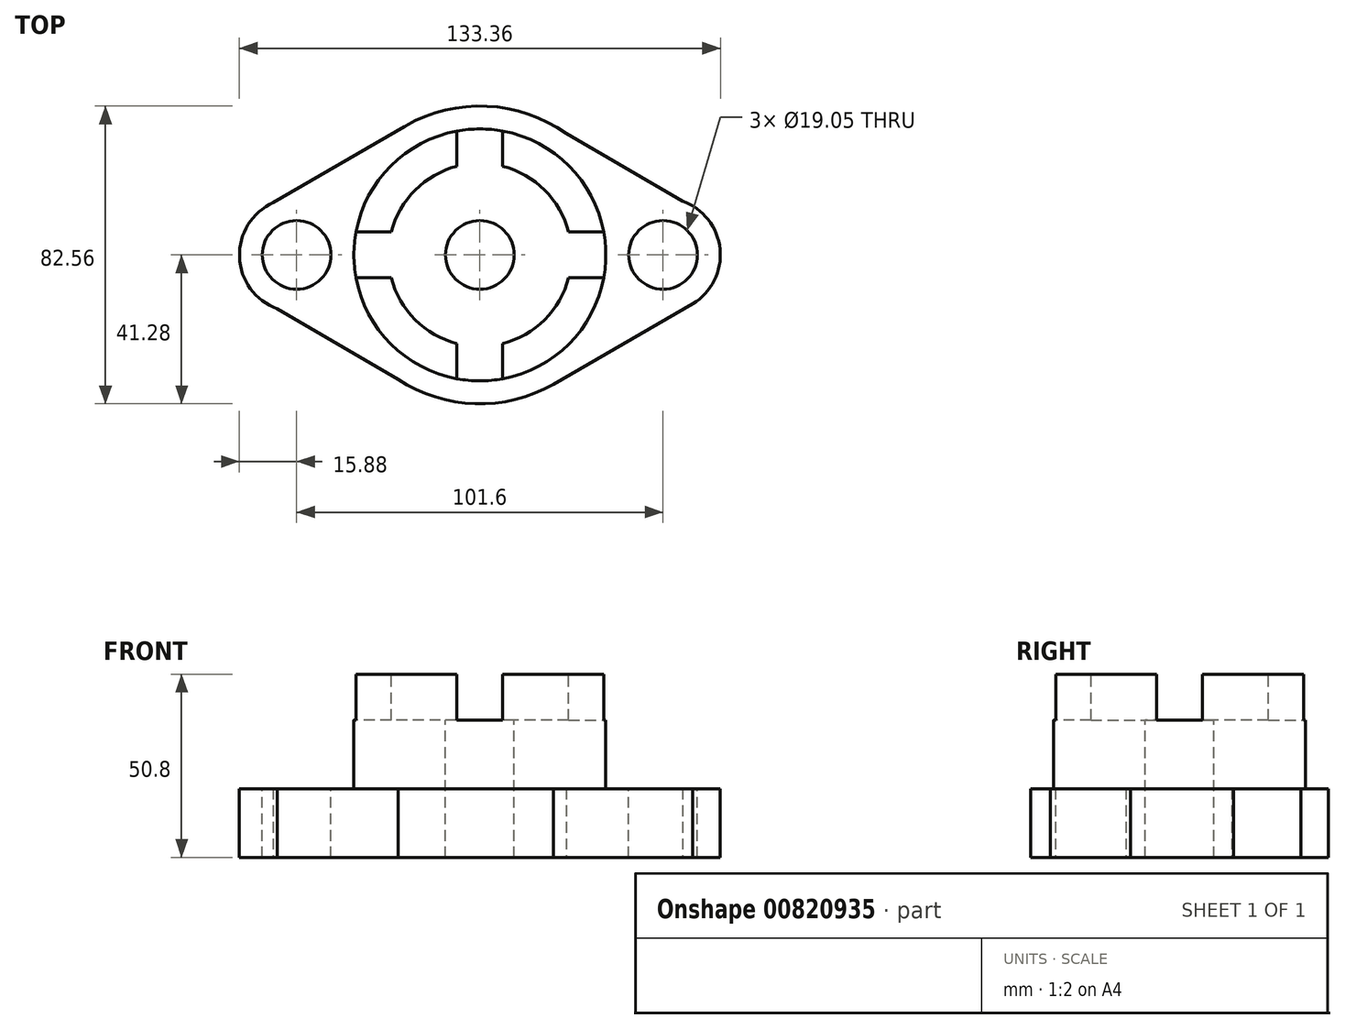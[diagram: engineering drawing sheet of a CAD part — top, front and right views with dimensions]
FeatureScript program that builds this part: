
annotation { "Feature Type Name" : "Feature", "Feature Type Description" : "" }
export const myFeature = defineFeature(function(context is Context, id is Id, definition is map)
    precondition{}
    {
        {
            var Q0;
            Q0=qCreatedBy(makeId("Top.planeOp"),FACE);
            var sketch = newSketch(context, id + "F0", { "sketchPlane" : qUnion([Q0])});
            skCircle(sketch, "E0", {"center": v(0, 0) * mm, "radius": 41.28 * mm});
            skSolve(sketch);
        }
        {
            var Q0;
            Q0=qCreatedBy(makeId("Top.planeOp"),FACE);
            var sketch = newSketch(context, id + "F1", { "sketchPlane" : qUnion([Q0])});
            skCircle(sketch, "E1", {"center": v(-50.8, 0) * mm, "radius": 15.88 * mm});
            skCircle(sketch, "E2", {"center": v(50.8, 0) * mm, "radius": 15.88 * mm});
            skSolve(sketch);
        }
        {
            var Q0;
            Q0=qCreatedBy(makeId("Top.planeOp"),FACE);
            var sketch = newSketch(context, id + "F2", { "sketchPlane" : qUnion([Q0])});
            skLineSegment(sketch, "E3", {"start": v(-60.13, 12.85) * mm, "end": v(-20.59, 35.77) * mm});
            skLineSegment(sketch, "E4", {"start": v(-20.59, 35.77) * mm, "end": v(-27.6, 7.86) * mm});
            skLineSegment(sketch, "E5", {"start": v(-27.6, 7.86) * mm, "end": v(-60.13, 12.85) * mm});
            skSolve(sketch);
        }
        {
            var Q0;
            Q0=qCreatedBy(makeId("Top.planeOp"),FACE);
            var sketch = newSketch(context, id + "F3", { "sketchPlane" : qUnion([Q0])});
            skLineSegment(sketch, "E6", {"start": v(-60.23, -12.58) * mm, "end": v(-21.62, -35.1) * mm});
            skLineSegment(sketch, "E7", {"start": v(-60.23, -12.58) * mm, "end": v(-30.25, -6.15) * mm});
            skLineSegment(sketch, "E8", {"start": v(-30.25, -6.15) * mm, "end": v(-21.62, -35.1) * mm});
            skSolve(sketch);
        }
        {
            var Q0;
            Q0=qCreatedBy(makeId("Top.planeOp"),FACE);
            var sketch = newSketch(context, id + "F4", { "sketchPlane" : qUnion([Q0])});
            skLineSegment(sketch, "E9", {"start": v(17.34, 37.46) * mm, "end": v(58.42, 13.63) * mm});
            skLineSegment(sketch, "E10", {"start": v(17.34, 37.46) * mm, "end": v(25.2, 3.74) * mm});
            skLineSegment(sketch, "E11", {"start": v(25.2, 3.74) * mm, "end": v(58.42, 13.63) * mm});
            skSolve(sketch);
        }
        {
            var Q0;
            Q0=qCreatedBy(makeId("Top.planeOp"),FACE);
            var sketch = newSketch(context, id + "F5", { "sketchPlane" : qUnion([Q0])});
            skLineSegment(sketch, "E12", {"start": v(16.99, -37.85) * mm, "end": v(60.11, -12.95) * mm});
            skLineSegment(sketch, "E13", {"start": v(20.37, -35.9) * mm, "end": v(28.45, -4.63) * mm});
            skLineSegment(sketch, "E14", {"start": v(28.45, -4.63) * mm, "end": v(59, -13.6) * mm});
            skSolve(sketch);
        }
        {
            var Q0;
            Q0=makeQuery(id+"F2.imprint","IMPRINT",FACE,{"disambiguationData":[TD([[makeQuery(id+"F2.imprint","IMPRINT",EDGE,{"derivedFrom":sQuery(id+"F2.wireOp",EDGE,"E3")}),-1.0]])]});
            var Q1;
            Q1=makeQuery(id+"F1.imprint","IMPRINT",FACE,{"disambiguationData":[TD([[makeQuery(id+"F1.imprint","IMPRINT",EDGE,{"derivedFrom":sQuery(id+"F1.wireOp",EDGE,"E1")}),1.0]])]});
            var Q2;
            Q2=makeQuery(id+"F0.imprint","IMPRINT",FACE,{"disambiguationData":[TD([[makeQuery(id+"F0.imprint","IMPRINT",EDGE,{"derivedFrom":sQuery(id+"F0.wireOp",EDGE,"E0")}),1.0]])]});
            var Q3;
            Q3=makeQuery(id+"F3.imprint","IMPRINT",FACE,{"disambiguationData":[TD([[makeQuery(id+"F3.imprint","IMPRINT",EDGE,{"derivedFrom":sQuery(id+"F3.wireOp",EDGE,"E6")}),1.0]])]});
            var Q4;
            Q4=makeQuery(id+"F4.imprint","IMPRINT",FACE,{"disambiguationData":[TD([[makeQuery(id+"F4.imprint","IMPRINT",EDGE,{"derivedFrom":sQuery(id+"F4.wireOp",EDGE,"E9")}),-1.0]])]});
            var Q5;
            Q5=makeQuery(id+"F1.imprint","IMPRINT",FACE,{"disambiguationData":[TD([[makeQuery(id+"F1.imprint","IMPRINT",EDGE,{"derivedFrom":sQuery(id+"F1.wireOp",EDGE,"E2")}),1.0]])]});
            var Q6;
            {var subQ0=sQuery(id+"F5.wireOp",EDGE,"E13");Q6=makeQuery(id+"F5.imprint","IMPRINT",FACE,{"disambiguationData":[TD([[makeQuery(id+"F5.imprint","IMPRINT",EDGE,{"derivedFrom":subQ0}),-1.0]])]});}
            extrude(context, id + "F6", {"entities" : qUnion([Q0, Q1, Q2, Q3, Q4, Q5, Q6]), "depth" : 19.05 * mm, "offsetDistance" : 25.4 * mm});
        }
        {
            var Q0;
            Q0=makeQuery(id+"F6.opExtrude","SWEPT_BODY",BODY,{"disambiguationData":[OSD([sQuery(id+"F2.wireOp",EDGE,"E3"),sQuery(id+"F2.wireOp",EDGE,"E4"),sQuery(id+"F2.wireOp",EDGE,"E5")])]});
            var Q1;
            Q1=makeQuery(id+"F6.opExtrude","SWEPT_BODY",BODY,{"disambiguationData":[OSD([sQuery(id+"F0.wireOp",EDGE,"E0")])]});
            var Q2;
            Q2=makeQuery(id+"F6.opExtrude","SWEPT_BODY",BODY,{"disambiguationData":[OSD([sQuery(id+"F3.wireOp",EDGE,"E6"),sQuery(id+"F3.wireOp",EDGE,"E7"),sQuery(id+"F3.wireOp",EDGE,"E8")])]});
            var Q3;
            Q3=makeQuery(id+"F6.opExtrude","SWEPT_BODY",BODY,{"disambiguationData":[OSD([sQuery(id+"F5.wireOp",EDGE,"E12"),sQuery(id+"F5.wireOp",EDGE,"E13"),sQuery(id+"F5.wireOp",EDGE,"E14")])]});
            var Q4;
            Q4=makeQuery(id+"F6.opExtrude","SWEPT_BODY",BODY,{"disambiguationData":[OSD([sQuery(id+"F4.wireOp",EDGE,"E9"),sQuery(id+"F4.wireOp",EDGE,"E10"),sQuery(id+"F4.wireOp",EDGE,"E11")])]});
            var Q5;
            Q5=makeQuery(id+"F6.opExtrude","SWEPT_BODY",BODY,{"disambiguationData":[OSD([sQuery(id+"F1.wireOp",EDGE,"E2")])]});
            var Q6;
            Q6=makeQuery(id+"F6.opExtrude","SWEPT_BODY",BODY,{"disambiguationData":[OSD([sQuery(id+"F1.wireOp",EDGE,"E1")])]});
            booleanBodies(context, id + "F7", {"operationType" : BooleanOperationType.UNION, "tools" : qUnion([Q0, Q1, Q2, Q3, Q4, Q5, Q6])});
        }
        {
            var Q0;
            Q0=makeQuery(id+"F7.opBoolean","MERGE",FACE,{"derivedFrom":[makeQuery(id+"F6.opExtrude","CAP_FACE",FACE,{"disambiguationData":[OSD([sQuery(id+"F0.wireOp",EDGE,"E0")])],"isStart":false}),makeQuery(id+"F6.opExtrude","CAP_FACE",FACE,{"disambiguationData":[OSD([sQuery(id+"F1.wireOp",EDGE,"E1")])],"isStart":false}),makeQuery(id+"F6.opExtrude","CAP_FACE",FACE,{"disambiguationData":[OSD([sQuery(id+"F1.wireOp",EDGE,"E2")])],"isStart":false}),makeQuery(id+"F6.opExtrude","CAP_FACE",FACE,{"disambiguationData":[OSD([sQuery(id+"F2.wireOp",EDGE,"E3"),sQuery(id+"F2.wireOp",EDGE,"E4"),sQuery(id+"F2.wireOp",EDGE,"E5")])],"isStart":false}),makeQuery(id+"F6.opExtrude","CAP_FACE",FACE,{"disambiguationData":[OSD([sQuery(id+"F3.wireOp",EDGE,"E6"),sQuery(id+"F3.wireOp",EDGE,"E7"),sQuery(id+"F3.wireOp",EDGE,"E8")])],"isStart":false}),makeQuery(id+"F6.opExtrude","CAP_FACE",FACE,{"disambiguationData":[OSD([sQuery(id+"F4.wireOp",EDGE,"E9"),sQuery(id+"F4.wireOp",EDGE,"E10"),sQuery(id+"F4.wireOp",EDGE,"E11")])],"isStart":false}),makeQuery(id+"F6.opExtrude","CAP_FACE",FACE,{"disambiguationData":[OSD([sQuery(id+"F5.wireOp",EDGE,"E12"),sQuery(id+"F5.wireOp",EDGE,"E13"),sQuery(id+"F5.wireOp",EDGE,"E14")])],"isStart":false})]});
            var sketch = newSketch(context, id + "F8", { "sketchPlane" : qUnion([Q0])});
            skCircle(sketch, "E15", {"center": v(0, 0) * mm, "radius": 34.93 * mm});
            skSolve(sketch);
        }
        {
            var Q0;
            Q0=makeQuery(id+"F8.imprint","IMPRINT",FACE,{"disambiguationData":[TD([[makeQuery(id+"F8.imprint","IMPRINT",EDGE,{"derivedFrom":sQuery(id+"F8.wireOp",EDGE,"E15")}),1.0]])]});
            extrude(context, id + "F9", {"entities" : qUnion([Q0]), "operationType" : NewBodyOperationType.ADD, "depth" : 31.75 * mm, "offsetDistance" : 25.4 * mm});
        }
        {
            var Q0;
            Q0=makeQuery(id+"F9.opExtrude","CAP_FACE",FACE,{"disambiguationData":[OSD([sQuery(id+"F8.wireOp",EDGE,"E15")])],"isStart":false});
            var sketch = newSketch(context, id + "F10", { "sketchPlane" : qUnion([Q0])});
            skCircle(sketch, "E16", {"center": v(0, 0) * mm, "radius": 25.4 * mm});
            skSolve(sketch);
        }
        {
            var Q0;
            Q0=makeQuery(id+"F10.imprint","IMPRINT",FACE,{"disambiguationData":[TD([[makeQuery(id+"F10.imprint","IMPRINT",EDGE,{"derivedFrom":sQuery(id+"F10.wireOp",EDGE,"E16")}),1.0]])]});
            extrude(context, id + "F11", {"entities" : qUnion([Q0]), "operationType" : NewBodyOperationType.REMOVE, "oppositeDirection" : true, "depth" : 12.7 * mm, "offsetDistance" : 25.4 * mm});
        }
        {
            var Q0;
            Q0=makeQuery(id+"F11.boolean.opBoolean","COPY",FACE,{"derivedFrom":makeQuery(id+"F11.opExtrude","CAP_FACE",FACE,{"disambiguationData":[OSD([sQuery(id+"F10.wireOp",EDGE,"E16")])],"isStart":false})});
            var sketch = newSketch(context, id + "F12", { "sketchPlane" : qUnion([Q0])});
            skCircle(sketch, "E17", {"center": v(0, 0) * mm, "radius": 9.53 * mm});
            skSolve(sketch);
        }
        {
            var Q0;
            Q0=makeQuery(id+"F12.imprint","IMPRINT",FACE,{"disambiguationData":[TD([[makeQuery(id+"F12.imprint","IMPRINT",EDGE,{"derivedFrom":sQuery(id+"F12.wireOp",EDGE,"E17")}),1.0]])]});
            extrude(context, id + "F13", {"entities" : qUnion([Q0]), "operationType" : NewBodyOperationType.REMOVE, "oppositeDirection" : true, "depth" : 50.8 * mm, "offsetDistance" : 25.4 * mm});
        }
        {
            var Q0;
            Q0=makeQuery(id+"F9.opExtrude","CAP_FACE",FACE,{"disambiguationData":[OSD([sQuery(id+"F8.wireOp",EDGE,"E15")])],"isStart":false});
            var sketch = newSketch(context, id + "F14", { "sketchPlane" : qUnion([Q0])});
            skLineSegment(sketch, "E18", {"start": v(-6.35, -24.6) * mm, "end": v(-6.35, -34.34) * mm});
            skLineSegment(sketch, "E19", {"start": v(6.35, -24.6) * mm, "end": v(6.35, -34.34) * mm});
            skLineSegment(sketch, "E20", {"start": v(-6.35, 34.34) * mm, "end": v(-6.35, 24.6) * mm});
            skLineSegment(sketch, "E21", {"start": v(6.35, 24.6) * mm, "end": v(6.35, 34.34) * mm});
            skLineSegment(sketch, "E22", {"start": v(24.6, 6.35) * mm, "end": v(34.34, 6.35) * mm});
            skLineSegment(sketch, "E23", {"start": v(24.6, -6.35) * mm, "end": v(34.34, -6.35) * mm});
            skLineSegment(sketch, "E24", {"start": v(-24.6, 6.35) * mm, "end": v(-34.34, 6.35) * mm});
            skLineSegment(sketch, "E25", {"start": v(-24.6, -6.35) * mm, "end": v(-34.34, -6.35) * mm});
            skSolve(sketch);
        }
        {
            var Q0;
            {var subQ0=sQuery(id+"F14.wireOp",EDGE,"E24");Q0=makeQuery(id+"F14.imprint","IMPRINT",FACE,{"disambiguationData":[TD([[makeQuery(id+"F14.imprint","IMPRINT",EDGE,{"derivedFrom":subQ0}),1.0]])]});}
            var Q1;
            {var subQ0=sQuery(id+"F14.wireOp",EDGE,"E20");Q1=makeQuery(id+"F14.imprint","IMPRINT",FACE,{"disambiguationData":[TD([[makeQuery(id+"F14.imprint","IMPRINT",EDGE,{"derivedFrom":subQ0}),1.0]])]});}
            var Q2;
            {var subQ0=sQuery(id+"F14.wireOp",EDGE,"E22");Q2=makeQuery(id+"F14.imprint","IMPRINT",FACE,{"disambiguationData":[TD([[makeQuery(id+"F14.imprint","IMPRINT",EDGE,{"derivedFrom":subQ0}),-1.0]])]});}
            var Q3;
            {var subQ0=sQuery(id+"F14.wireOp",EDGE,"E18");Q3=makeQuery(id+"F14.imprint","IMPRINT",FACE,{"disambiguationData":[TD([[makeQuery(id+"F14.imprint","IMPRINT",EDGE,{"derivedFrom":subQ0}),1.0]])]});}
            extrude(context, id + "F15", {"entities" : qUnion([Q0, Q1, Q2, Q3]), "operationType" : NewBodyOperationType.REMOVE, "oppositeDirection" : true, "depth" : 12.7 * mm, "offsetDistance" : 25.4 * mm});
        }
        {
            var Q0;
            Q0=makeQuery(id+"F7.opBoolean","MERGE",FACE,{"derivedFrom":[makeQuery(id+"F6.opExtrude","CAP_FACE",FACE,{"disambiguationData":[OSD([sQuery(id+"F0.wireOp",EDGE,"E0")])],"isStart":false}),makeQuery(id+"F6.opExtrude","CAP_FACE",FACE,{"disambiguationData":[OSD([sQuery(id+"F1.wireOp",EDGE,"E1")])],"isStart":false}),makeQuery(id+"F6.opExtrude","CAP_FACE",FACE,{"disambiguationData":[OSD([sQuery(id+"F1.wireOp",EDGE,"E2")])],"isStart":false}),makeQuery(id+"F6.opExtrude","CAP_FACE",FACE,{"disambiguationData":[OSD([sQuery(id+"F2.wireOp",EDGE,"E3"),sQuery(id+"F2.wireOp",EDGE,"E4"),sQuery(id+"F2.wireOp",EDGE,"E5")])],"isStart":false}),makeQuery(id+"F6.opExtrude","CAP_FACE",FACE,{"disambiguationData":[OSD([sQuery(id+"F3.wireOp",EDGE,"E6"),sQuery(id+"F3.wireOp",EDGE,"E7"),sQuery(id+"F3.wireOp",EDGE,"E8")])],"isStart":false}),makeQuery(id+"F6.opExtrude","CAP_FACE",FACE,{"disambiguationData":[OSD([sQuery(id+"F4.wireOp",EDGE,"E9"),sQuery(id+"F4.wireOp",EDGE,"E10"),sQuery(id+"F4.wireOp",EDGE,"E11")])],"isStart":false}),makeQuery(id+"F6.opExtrude","CAP_FACE",FACE,{"disambiguationData":[OSD([sQuery(id+"F5.wireOp",EDGE,"E12"),sQuery(id+"F5.wireOp",EDGE,"E13"),sQuery(id+"F5.wireOp",EDGE,"E14")])],"isStart":false})]});
            var sketch = newSketch(context, id + "F16", { "sketchPlane" : qUnion([Q0])});
            skCircle(sketch, "E26", {"center": v(-50.8, 0) * mm, "radius": 9.53 * mm});
            skCircle(sketch, "E27", {"center": v(50.8, 0) * mm, "radius": 9.53 * mm});
            skSolve(sketch);
        }
        {
            var Q0;
            Q0=makeQuery(id+"F16.imprint","IMPRINT",FACE,{"disambiguationData":[TD([[makeQuery(id+"F16.imprint","IMPRINT",EDGE,{"derivedFrom":sQuery(id+"F16.wireOp",EDGE,"E26")}),1.0]])]});
            var Q1;
            Q1=makeQuery(id+"F16.imprint","IMPRINT",FACE,{"disambiguationData":[TD([[makeQuery(id+"F16.imprint","IMPRINT",EDGE,{"derivedFrom":sQuery(id+"F16.wireOp",EDGE,"E27")}),1.0]])]});
            extrude(context, id + "F17", {"entities" : qUnion([Q0, Q1]), "operationType" : NewBodyOperationType.REMOVE, "oppositeDirection" : true, "depth" : 25.4 * mm, "offsetDistance" : 25.4 * mm});
        }
    });
